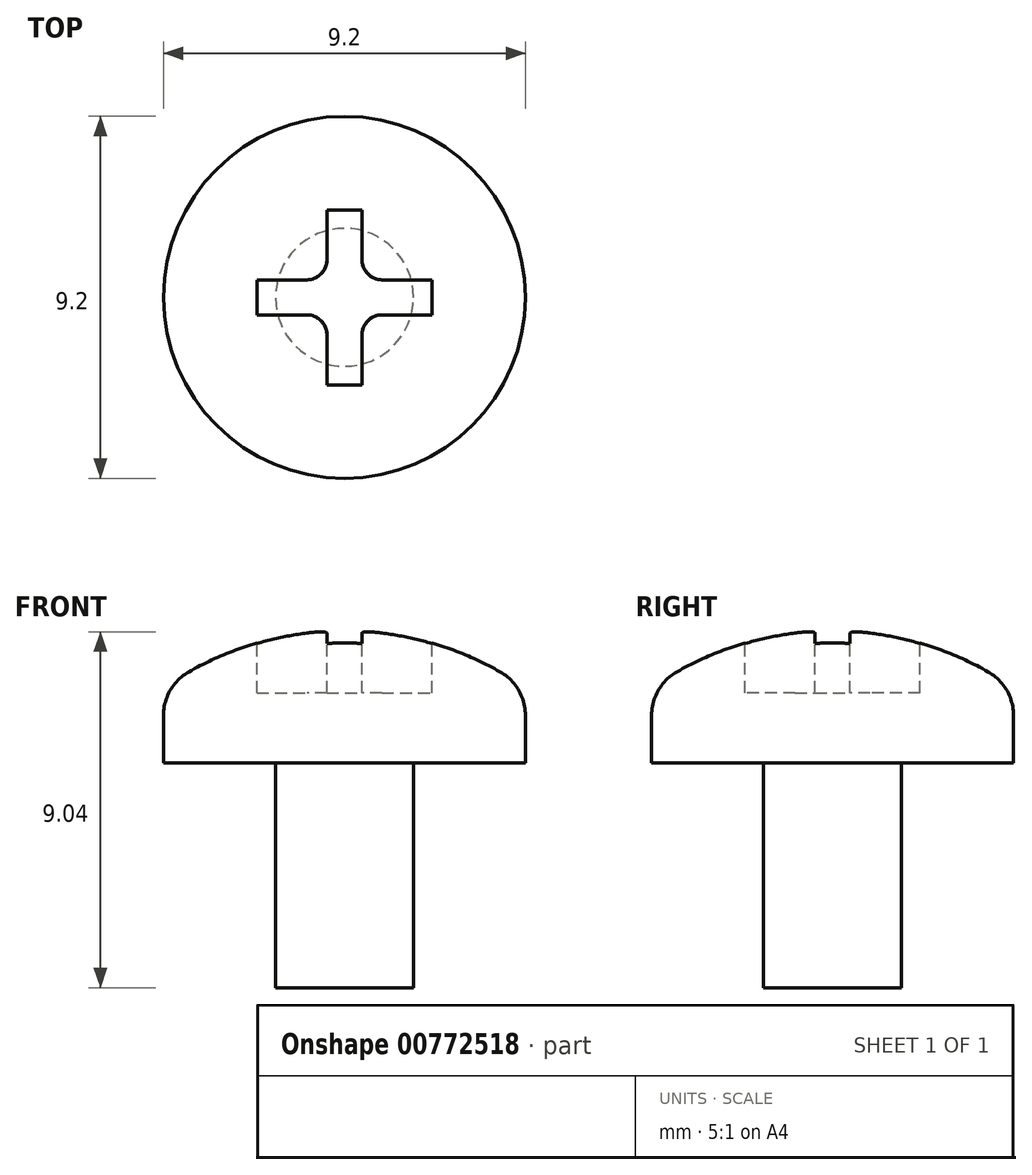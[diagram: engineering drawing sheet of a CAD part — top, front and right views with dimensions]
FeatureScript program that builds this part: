
annotation { "Feature Type Name" : "Feature", "Feature Type Description" : "" }
export const myFeature = defineFeature(function(context is Context, id is Id, definition is map)
    precondition{}
    {
        {
            var Q0;
            Q0=qCreatedBy(makeId("Top.planeOp"),FACE);
            var sketch = newSketch(context, id + "F0", { "sketchPlane" : qUnion([Q0])});
            skCircle(sketch, "E0", {"center": v(0, 0) * mm, "radius": 1.75 * mm});
            skSolve(sketch);
        }
        {
            var Q0;
            Q0=qSketchRegion(id+"F0",true);
            extrude(context, id + "F1", {"entities" : qUnion([Q0]), "depth" : 5.7 * mm});
        }
        {
            var Q0;
            Q0=qCreatedBy(makeId("Right.planeOp"),FACE);
            var sketch = newSketch(context, id + "F2", { "sketchPlane" : qUnion([Q0])});
            skLineSegment(sketch, "E1", {"start": v(-4.6, 5.72) * mm, "end": v(0, 5.72) * mm});
            skLineSegment(sketch, "E2", {"start": v(0, 0) * mm, "end": v(0, 9.1) * mm, "construction": true});
            skLineSegment(sketch, "E3", {"start": v(0, 5.72) * mm, "end": v(0, 9.1) * mm});
            skLineSegment(sketch, "E4", {"start": v(-4.6, 5.72) * mm, "end": v(-4.6, 7.62) * mm});
            skArc(sketch, "E5", {"start": v(0, 9.1) * mm, "mid": v(-2.4, 8.7) * mm, "end": v(-4.6, 7.62) * mm});
            skSolve(sketch);
        }
        {
            var Q0;
            Q0=qSketchRegion(id+"F2",true);
            var Q1;
            Q1=sQuery(id+"F2.wireOp",EDGE,"E2");
            revolve(context, id + "F3", {"operationType" : NewBodyOperationType.ADD, "entities" : qUnion([Q0]), "axis" : qUnion([Q1]), "revolveType" : RevolveType.FULL});
        }
        {
            var Q0;
            Q0=makeQuery(id+"F3.opRevolve","SWEPT_EDGE",EDGE,{"disambiguationData":[OSD([sQuery(id+"F2.wireOp",EDGE,"E4"),sQuery(id+"F2.wireOp",EDGE,"E5")])]});
            fillet(context, id + "F4", {"entities" : qUnion([Q0]), "radius" : 1.27 * mm, "tangentPropagation" : true, "allowEdgeOverflow" : false});
        }
        {
            var Q0;
            Q0=qCreatedBy(makeId("Top.planeOp"),FACE);
            cPlane(context, id + "F5", {"entities" : qUnion([Q0]), "cplaneType" : CPlaneType.OFFSET, "offset" : 10.4 * mm, "width" : 152.4 * mm, "height" : 152.4 * mm});
        }
        {
            var Q0;
            Q0=qCreatedBy(id+"F5.planeOp",FACE);
            var sketch = newSketch(context, id + "F6", { "sketchPlane" : qUnion([Q0])});
            skLineSegment(sketch, "E6.bottom", {"start": v(-2.22, -0.44) * mm, "end": v(-0.44, -0.44) * mm});
            skLineSegment(sketch, "E6.top", {"start": v(-2.22, 0.44) * mm, "end": v(-0.44, 0.44) * mm});
            skLineSegment(sketch, "E6.left", {"start": v(-2.22, -0.44) * mm, "end": v(-2.22, 0.44) * mm});
            skLineSegment(sketch, "E6.right", {"start": v(2.22, -0.44) * mm, "end": v(2.22, 0.44) * mm});
            skLineSegment(sketch, "E7.bottom", {"start": v(-0.44, 2.22) * mm, "end": v(0.44, 2.22) * mm});
            skLineSegment(sketch, "E7.top", {"start": v(-0.44, -2.22) * mm, "end": v(0.44, -2.22) * mm});
            skLineSegment(sketch, "E7.left", {"start": v(-0.44, 2.22) * mm, "end": v(-0.44, 0.44) * mm});
            skLineSegment(sketch, "E7.right", {"start": v(0.44, 2.22) * mm, "end": v(0.44, 0.44) * mm});
            skLineSegment(sketch, "E8.trimOffspring", {"start": v(-0.44, -0.44) * mm, "end": v(-0.44, -2.22) * mm});
            skLineSegment(sketch, "E9.trimOffspring", {"start": v(0.44, -0.44) * mm, "end": v(2.22, -0.44) * mm});
            skLineSegment(sketch, "E10.trimOffspring", {"start": v(0.44, -0.44) * mm, "end": v(0.44, -2.22) * mm});
            skLineSegment(sketch, "E11.trimOffspring", {"start": v(0.44, 0.44) * mm, "end": v(2.22, 0.44) * mm});
            skLineSegment(sketch, "E12", {"start": v(0, -2.22) * mm, "end": v(0, 2.22) * mm, "construction": true});
            skPoint(sketch, "E12.endSnap0", {"position": v(0, 2.22) * mm});
            skLineSegment(sketch, "E13", {"start": v(-2.22, 0) * mm, "end": v(2.22, 0) * mm, "construction": true});
            skSolve(sketch);
        }
        {
            var Q0;
            Q0=qSketchRegion(id+"F6",true);
            extrude(context, id + "F7", {"entities" : qUnion([Q0]), "operationType" : NewBodyOperationType.REMOVE, "oppositeDirection" : true, "depth" : 2.92 * mm});
        }
        {
            var Q0;
            Q0=makeQuery(id+"F7.boolean.opBoolean","COPY",EDGE,{"derivedFrom":makeQuery(id+"F7.opExtrude","SWEPT_EDGE",EDGE,{"disambiguationData":[OSD([sQuery(id+"F6.wireOp",EDGE,"E6.top"),sQuery(id+"F6.wireOp",EDGE,"E7.left")])]})});
            var Q1;
            Q1=makeQuery(id+"F7.boolean.opBoolean","COPY",EDGE,{"derivedFrom":makeQuery(id+"F7.opExtrude","SWEPT_EDGE",EDGE,{"disambiguationData":[OSD([sQuery(id+"F6.wireOp",EDGE,"E7.right"),sQuery(id+"F6.wireOp",EDGE,"E11.trimOffspring")])]})});
            var Q2;
            Q2=makeQuery(id+"F7.boolean.opBoolean","COPY",EDGE,{"derivedFrom":makeQuery(id+"F7.opExtrude","SWEPT_EDGE",EDGE,{"disambiguationData":[OSD([sQuery(id+"F6.wireOp",EDGE,"E6.bottom"),sQuery(id+"F6.wireOp",EDGE,"E8.trimOffspring")])]})});
            var Q3;
            Q3=makeQuery(id+"F7.boolean.opBoolean","COPY",EDGE,{"derivedFrom":makeQuery(id+"F7.opExtrude","SWEPT_EDGE",EDGE,{"disambiguationData":[OSD([sQuery(id+"F6.wireOp",EDGE,"E9.trimOffspring"),sQuery(id+"F6.wireOp",EDGE,"E10.trimOffspring")])]})});
            fillet(context, id + "F8", {"entities" : qUnion([Q0, Q1, Q2, Q3]), "radius" : 0.5 * mm, "tangentPropagation" : true, "allowEdgeOverflow" : false});
        }
    });
